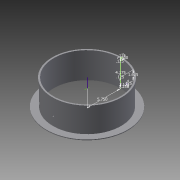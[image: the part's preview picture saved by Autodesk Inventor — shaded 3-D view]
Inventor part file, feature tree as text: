
AUTODESK INVENTOR PART (.ipt)
format: ipt  version: 2015 (Build 190159000, 159)  size: 118,784 bytes
history: native  units: in
note: dims shown in document units (in); Inventor stores cm internally (conversion verified against a paired STEP export)
features: sketch x2, revolve x1, plane x1, hole x1
ambient origin geometry x8: Origin, YZ Plane, XZ Plane, XY Plane, X Axis, Y Axis, Z Axis, Center Point
bodies: Solid1 (feature_tree)
feature tree (5):
  revolve  "Revolution1"  [1 undecoded]
  plane  "Work Plane1"
  hole  "Hole1"  [1 undecoded]
  sketch  "Sketch1"  dims[d0=1.25in d1=0.125in]
  sketch  "Sketch2"  dims[d2=1.125in d3=4.375in d4=0.125in d5=5.75in d6=90.0deg d7=0.125in d8=0.5in d9=1.625in d10=0.275in d11=0.75in d12=0.375in d13=0.25in d14=0.5635in d15=1.0in d16=0.8108in d17=0.125in]
note: 2 required parameter values undecoded (feature->parameter linkage not recoverable at this tier; creation-order binding heuristic only, values carry confidence <= 0.55)